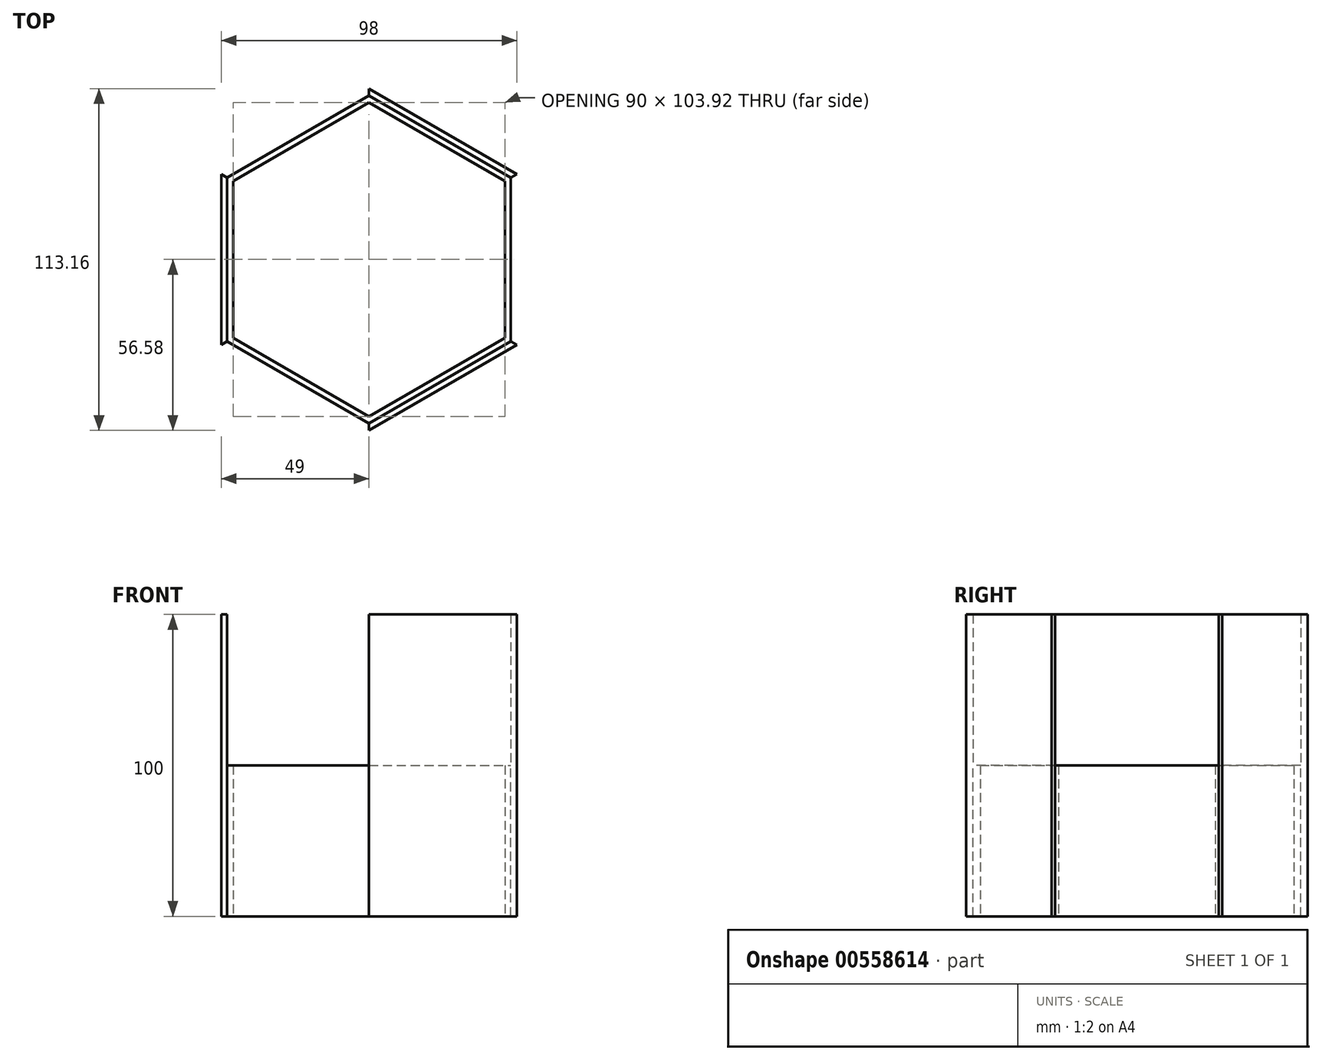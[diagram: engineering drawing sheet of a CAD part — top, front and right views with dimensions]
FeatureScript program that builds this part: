
annotation { "Feature Type Name" : "Feature", "Feature Type Description" : "" }
export const myFeature = defineFeature(function(context is Context, id is Id, definition is map)
    precondition{}
    {
        {
            var Q0;
            Q0=qCreatedBy(makeId("Top.planeOp"),FACE);
            var sketch = newSketch(context, id + "F0", { "sketchPlane" : qUnion([Q0])});
            skCircle(sketch, "E0.cCircle", {"center": v(0, 0) * mm, "radius": 45 * mm, "construction": true});
            skLineSegment(sketch, "E0.0", {"start": v(-45, -25.98) * mm, "end": v(-45, 25.98) * mm});
            skLineSegment(sketch, "E0.1", {"start": v(-45, 25.98) * mm, "end": v(0, 51.96) * mm});
            skLineSegment(sketch, "E0.2", {"start": v(0, 51.96) * mm, "end": v(45, 25.98) * mm});
            skLineSegment(sketch, "E0.3", {"start": v(45, 25.98) * mm, "end": v(45, -25.98) * mm});
            skLineSegment(sketch, "E0.4", {"start": v(45, -25.98) * mm, "end": v(0, -51.96) * mm});
            skLineSegment(sketch, "E0.5", {"start": v(0, -51.96) * mm, "end": v(-45, -25.98) * mm});
            skPoint(sketch, "E0.0.midPoint", {"position": v(-45, 0) * mm});
            skLineSegment(sketch, "E1.0", {"start": v(-49, -28.3) * mm, "end": v(-49, 28.3) * mm});
            skLineSegment(sketch, "E1.1", {"start": v(0, 56.58) * mm, "end": v(49, 28.3) * mm});
            skLineSegment(sketch, "E1.2", {"start": v(49, 28.3) * mm, "end": v(49, -28.3) * mm});
            skLineSegment(sketch, "E1.3", {"start": v(-49, 28.3) * mm, "end": v(0, 56.58) * mm});
            skLineSegment(sketch, "E1.4", {"start": v(49, -28.3) * mm, "end": v(0, -56.58) * mm});
            skLineSegment(sketch, "E1.5", {"start": v(0, -56.58) * mm, "end": v(-49, -28.3) * mm});
            skSolve(sketch);
        }
        {
            var Q0;
            Q0=makeQuery(id+"F0.imprint","IMPRINT",FACE,{"disambiguationData":[TD([[makeQuery(id+"F0.imprint","IMPRINT",EDGE,{"derivedFrom":sQuery(id+"F0.wireOp",EDGE,"E0.0")}),1.0]])]});
            extrude(context, id + "F1", {"entities" : qUnion([Q0]), "depth" : 50 * mm, "offsetDistance" : 25 * mm});
        }
        {
            var Q0;
            Q0=makeQuery(id+"F1.opExtrude","CAP_FACE",FACE,{"disambiguationData":[OSD([sQuery(id+"F0.wireOp",EDGE,"E0.0"),sQuery(id+"F0.wireOp",EDGE,"E0.1"),sQuery(id+"F0.wireOp",EDGE,"E0.2"),sQuery(id+"F0.wireOp",EDGE,"E0.3"),sQuery(id+"F0.wireOp",EDGE,"E0.4"),sQuery(id+"F0.wireOp",EDGE,"E0.5"),sQuery(id+"F0.wireOp",EDGE,"E1.0"),sQuery(id+"F0.wireOp",EDGE,"E1.1"),sQuery(id+"F0.wireOp",EDGE,"E1.2"),sQuery(id+"F0.wireOp",EDGE,"E1.3"),sQuery(id+"F0.wireOp",EDGE,"E1.4"),sQuery(id+"F0.wireOp",EDGE,"E1.5")])],"isStart":false});
            var sketch = newSketch(context, id + "F2", { "sketchPlane" : qUnion([Q0])});
            skLineSegment(sketch, "E2", {"start": v(-49, 28.3) * mm, "end": v(0, 56.58) * mm});
            skLineSegment(sketch, "E3", {"start": v(0, 54.27) * mm, "end": v(-47, 27.14) * mm});
            skLineSegment(sketch, "E4.1.0", {"start": v(-49, -28.3) * mm, "end": v(-49, 28.3) * mm});
            skLineSegment(sketch, "E4.1.1", {"start": v(-47, -27.14) * mm, "end": v(-49, -28.3) * mm});
            skLineSegment(sketch, "E4.1.2", {"start": v(-47, 27.14) * mm, "end": v(-47, -27.14) * mm});
            skLineSegment(sketch, "E4.1.3", {"start": v(-49, 28.3) * mm, "end": v(-47, 27.14) * mm});
            skLineSegment(sketch, "E4.2.0", {"start": v(0, -56.58) * mm, "end": v(-49, -28.3) * mm});
            skLineSegment(sketch, "E4.2.1", {"start": v(0, -54.27) * mm, "end": v(0, -56.58) * mm});
            skLineSegment(sketch, "E4.2.2", {"start": v(-47, -27.14) * mm, "end": v(0, -54.27) * mm});
            skLineSegment(sketch, "E4.2.3", {"start": v(-49, -28.3) * mm, "end": v(-47, -27.14) * mm});
            skLineSegment(sketch, "E4.3.0", {"start": v(49, -28.3) * mm, "end": v(0, -56.58) * mm});
            skLineSegment(sketch, "E4.3.1", {"start": v(47, -27.14) * mm, "end": v(49, -28.3) * mm});
            skLineSegment(sketch, "E4.3.2", {"start": v(0, -54.27) * mm, "end": v(47, -27.14) * mm});
            skLineSegment(sketch, "E4.3.3", {"start": v(0, -56.58) * mm, "end": v(0, -54.27) * mm});
            skLineSegment(sketch, "E4.4.0", {"start": v(49, 28.3) * mm, "end": v(49, -28.3) * mm});
            skLineSegment(sketch, "E4.4.1", {"start": v(47, 27.14) * mm, "end": v(49, 28.3) * mm});
            skLineSegment(sketch, "E4.4.2", {"start": v(47, -27.14) * mm, "end": v(47, 27.14) * mm});
            skLineSegment(sketch, "E4.4.3", {"start": v(49, -28.3) * mm, "end": v(47, -27.14) * mm});
            skLineSegment(sketch, "E4.5.0", {"start": v(0, 56.58) * mm, "end": v(49, 28.3) * mm});
            skLineSegment(sketch, "E4.5.3", {"start": v(49, 28.3) * mm, "end": v(47, 27.14) * mm});
            skPoint(sketch, "E4.center", {"position": v(0, 0) * mm});
            skLineSegment(sketch, "E5", {"start": v(0, 56.58) * mm, "end": v(0, 54.27) * mm});
            skLineSegment(sketch, "E6", {"start": v(-45, 25.98) * mm, "end": v(-49, 28.3) * mm, "construction": true});
            skSolve(sketch);
        }
        {
            var Q0;
            Q0=makeQuery(id+"F2.imprint","IMPRINT",FACE,{"disambiguationData":[TD([[makeQuery(id+"F2.imprint","IMPRINT",EDGE,{"derivedFrom":sQuery(id+"F2.wireOp",EDGE,"E2")}),-1.0]])]});
            var Q1;
            Q1=makeQuery(id+"F2.imprint","IMPRINT",FACE,{"disambiguationData":[TD([[makeQuery(id+"F2.imprint","IMPRINT",EDGE,{"derivedFrom":sQuery(id+"F2.wireOp",EDGE,"E4.4.0")}),-1.0]])]});
            var Q2;
            Q2=makeQuery(id+"F2.imprint","IMPRINT",FACE,{"disambiguationData":[TD([[makeQuery(id+"F2.imprint","IMPRINT",EDGE,{"derivedFrom":sQuery(id+"F2.wireOp",EDGE,"E4.2.0")}),-1.0]])]});
            extrude(context, id + "F3", {"entities" : qUnion([Q0, Q1, Q2]), "operationType" : NewBodyOperationType.REMOVE, "endBound" : BoundingType.THROUGH_ALL, "oppositeDirection" : true, "depth" : 25 * mm, "offsetDistance" : 25 * mm});
        }
        {
            var Q0;
            Q0=makeQuery(id+"F1.opExtrude","CAP_FACE",FACE,{"disambiguationData":[OSD([sQuery(id+"F0.wireOp",EDGE,"E0.0"),sQuery(id+"F0.wireOp",EDGE,"E0.1"),sQuery(id+"F0.wireOp",EDGE,"E0.2"),sQuery(id+"F0.wireOp",EDGE,"E0.3"),sQuery(id+"F0.wireOp",EDGE,"E0.4"),sQuery(id+"F0.wireOp",EDGE,"E0.5"),sQuery(id+"F0.wireOp",EDGE,"E1.0"),sQuery(id+"F0.wireOp",EDGE,"E1.1"),sQuery(id+"F0.wireOp",EDGE,"E1.2"),sQuery(id+"F0.wireOp",EDGE,"E1.3"),sQuery(id+"F0.wireOp",EDGE,"E1.4"),sQuery(id+"F0.wireOp",EDGE,"E1.5")])],"isStart":false});
            var sketch = newSketch(context, id + "F4", { "sketchPlane" : qUnion([Q0])});
            skLineSegment(sketch, "E7", {"start": v(-49, 28.3) * mm, "end": v(0, 56.58) * mm});
            skLineSegment(sketch, "E8", {"start": v(0, 54.27) * mm, "end": v(-47, 27.14) * mm});
            skLineSegment(sketch, "E9.1.0", {"start": v(-49, -28.3) * mm, "end": v(-49, 28.3) * mm});
            skLineSegment(sketch, "E9.1.1", {"start": v(-47, -27.14) * mm, "end": v(-49, -28.3) * mm});
            skLineSegment(sketch, "E9.1.2", {"start": v(-47, 27.14) * mm, "end": v(-47, -27.14) * mm});
            skLineSegment(sketch, "E9.1.3", {"start": v(-49, 28.3) * mm, "end": v(-47, 27.14) * mm});
            skLineSegment(sketch, "E9.2.0", {"start": v(0, -56.58) * mm, "end": v(-49, -28.3) * mm});
            skLineSegment(sketch, "E9.2.1", {"start": v(0, -54.27) * mm, "end": v(0, -56.58) * mm});
            skLineSegment(sketch, "E9.2.2", {"start": v(-47, -27.14) * mm, "end": v(0, -54.27) * mm});
            skLineSegment(sketch, "E9.2.3", {"start": v(-49, -28.3) * mm, "end": v(-47, -27.14) * mm});
            skLineSegment(sketch, "E9.3.0", {"start": v(49, -28.3) * mm, "end": v(0, -56.58) * mm});
            skLineSegment(sketch, "E9.3.1", {"start": v(47, -27.14) * mm, "end": v(49, -28.3) * mm});
            skLineSegment(sketch, "E9.3.2", {"start": v(0, -54.27) * mm, "end": v(47, -27.14) * mm});
            skLineSegment(sketch, "E9.3.3", {"start": v(0, -56.58) * mm, "end": v(0, -54.27) * mm});
            skLineSegment(sketch, "E9.4.0", {"start": v(49, 28.3) * mm, "end": v(49, -28.3) * mm});
            skLineSegment(sketch, "E9.4.1", {"start": v(47, 27.14) * mm, "end": v(49, 28.3) * mm});
            skLineSegment(sketch, "E9.4.2", {"start": v(47, -27.14) * mm, "end": v(47, 27.14) * mm});
            skLineSegment(sketch, "E9.4.3", {"start": v(49, -28.3) * mm, "end": v(47, -27.14) * mm});
            skLineSegment(sketch, "E9.5.0", {"start": v(0, 56.58) * mm, "end": v(49, 28.3) * mm});
            skLineSegment(sketch, "E9.5.3", {"start": v(49, 28.3) * mm, "end": v(47, 27.14) * mm});
            skPoint(sketch, "E9.center", {"position": v(0, 0) * mm});
            skLineSegment(sketch, "E10", {"start": v(0, 56.58) * mm, "end": v(0, 54.27) * mm});
            skLineSegment(sketch, "E11", {"start": v(-45, 25.98) * mm, "end": v(-49, 28.3) * mm, "construction": true});
            skLineSegment(sketch, "E12", {"start": v(0, 54.27) * mm, "end": v(47, 27.14) * mm});
            skSolve(sketch);
        }
        {
            var Q0;
            Q0=makeQuery(id+"F4.imprint","IMPRINT",FACE,{"disambiguationData":[TD([[makeQuery(id+"F4.imprint","IMPRINT",EDGE,{"derivedFrom":sQuery(id+"F4.wireOp",EDGE,"E9.1.0")}),-1.0]])]});
            var Q1;
            Q1=makeQuery(id+"F4.imprint","IMPRINT",FACE,{"disambiguationData":[TD([[makeQuery(id+"F4.imprint","IMPRINT",EDGE,{"derivedFrom":sQuery(id+"F4.wireOp",EDGE,"E9.5.0")}),-1.0]])]});
            var Q2;
            Q2=makeQuery(id+"F4.imprint","IMPRINT",FACE,{"disambiguationData":[TD([[makeQuery(id+"F4.imprint","IMPRINT",EDGE,{"derivedFrom":sQuery(id+"F4.wireOp",EDGE,"E9.3.0")}),-1.0]])]});
            extrude(context, id + "F5", {"entities" : qUnion([Q0, Q1, Q2]), "operationType" : NewBodyOperationType.ADD, "depth" : 50 * mm, "offsetDistance" : 25 * mm});
        }
    });
